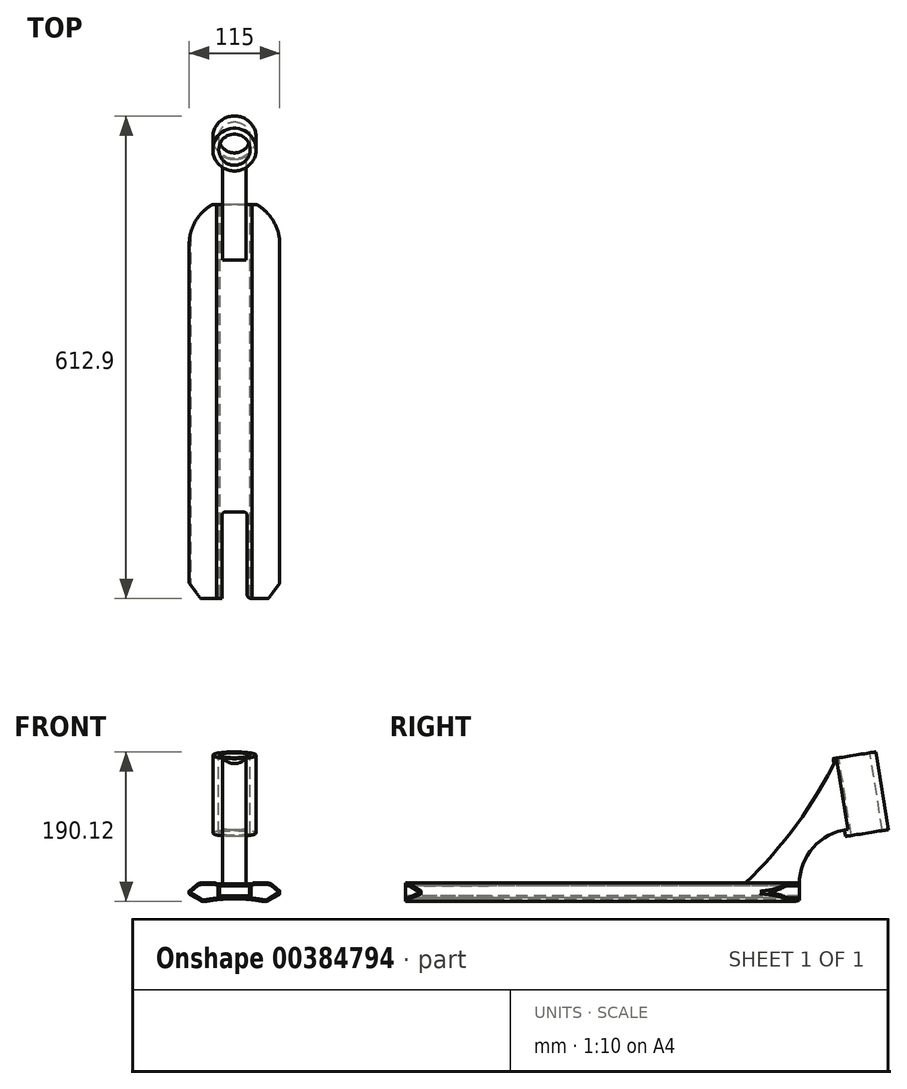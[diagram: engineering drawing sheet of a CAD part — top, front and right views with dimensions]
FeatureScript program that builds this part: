
annotation { "Feature Type Name" : "Feature", "Feature Type Description" : "" }
export const myFeature = defineFeature(function(context is Context, id is Id, definition is map)
    precondition{}
    {
        {
            var Q0;
            Q0=qCreatedBy(makeId("Front.planeOp"),FACE);
            var sketch = newSketch(context, id + "F0", { "sketchPlane" : qUnion([Q0])});
            skLineSegment(sketch, "E0", {"start": v(0, 0) * mm, "end": v(0, 7.07) * mm, "construction": true});
            skLineSegment(sketch, "E1", {"start": v(0, 13.8) * mm, "end": v(22.5, 13.8) * mm});
            skLineSegment(sketch, "E2", {"start": v(22.5, 13.8) * mm, "end": v(22.5, 15.1) * mm});
            skLineSegment(sketch, "E3", {"start": v(22.5, 15.1) * mm, "end": v(45.58, 15.1) * mm});
            skLineSegment(sketch, "E4", {"start": v(45.58, 15.1) * mm, "end": v(57.5, 5.1) * mm});
            skLineSegment(sketch, "E5", {"start": v(57.5, 5.1) * mm, "end": v(57.5, 1.1) * mm});
            skLineSegment(sketch, "E6", {"start": v(57.5, 1.1) * mm, "end": v(40.18, -8.9) * mm});
            skLineSegment(sketch, "E7.MirrorCS", {"start": v(0, 13.8) * mm, "end": v(-22.5, 13.8) * mm});
            skLineSegment(sketch, "E8.MirrorCS", {"start": v(-22.5, 13.8) * mm, "end": v(-22.5, 15.1) * mm});
            skLineSegment(sketch, "E9.MirrorCS", {"start": v(-22.5, 15.1) * mm, "end": v(-45.58, 15.1) * mm});
            skLineSegment(sketch, "E10.MirrorCS", {"start": v(-45.58, 15.1) * mm, "end": v(-57.5, 5.1) * mm});
            skLineSegment(sketch, "E11.MirrorCS", {"start": v(-57.5, 5.1) * mm, "end": v(-57.5, 1.1) * mm});
            skLineSegment(sketch, "E12.MirrorCS", {"start": v(-57.5, 1.1) * mm, "end": v(-40.18, -8.9) * mm});
            skArc(sketch, "E13", {"start": v(40.18, -8.9) * mm, "mid": v(0, -4.83) * mm, "end": v(-40.18, -8.9) * mm});
            skSolve(sketch);
        }
        {
            var Q0;
            Q0 = qSketchRegion(id + "F0", true);
            extrude(context, id + "F1", {"entities" : qUnion([Q0]), "endBound" : BoundingType.SYMMETRIC, "depth" : 500 * mm});
        }
        {
            var Q0;
            Q0=makeQuery(id+"F1.opExtrude","CAP_FACE",FACE,{"disambiguationData":[OSD([sQuery(id+"F0.wireOp",EDGE,"E1"),sQuery(id+"F0.wireOp",EDGE,"E2"),sQuery(id+"F0.wireOp",EDGE,"E3"),sQuery(id+"F0.wireOp",EDGE,"E4"),sQuery(id+"F0.wireOp",EDGE,"E5"),sQuery(id+"F0.wireOp",EDGE,"E6"),sQuery(id+"F0.wireOp",EDGE,"E7.MirrorCS"),sQuery(id+"F0.wireOp",EDGE,"E8.MirrorCS"),sQuery(id+"F0.wireOp",EDGE,"E9.MirrorCS"),sQuery(id+"F0.wireOp",EDGE,"E10.MirrorCS"),sQuery(id+"F0.wireOp",EDGE,"E11.MirrorCS"),sQuery(id+"F0.wireOp",EDGE,"E12.MirrorCS"),sQuery(id+"F0.wireOp",EDGE,"E13")])],"isStart":false});
            var sketch = newSketch(context, id + "F2", { "sketchPlane" : qUnion([Q0])});
            skLineSegment(sketch, "E14.bottom", {"start": v(-19, 11.8) * mm, "end": v(19, 11.8) * mm});
            skLineSegment(sketch, "E14.top", {"start": v(-19, -1.2) * mm, "end": v(19, -1.2) * mm});
            skLineSegment(sketch, "E14.left", {"start": v(-19, 11.8) * mm, "end": v(-19, -1.2) * mm});
            skLineSegment(sketch, "E14.right", {"start": v(19, 11.8) * mm, "end": v(19, -1.2) * mm});
            skSolve(sketch);
        }
        {
            var Q0;
            Q0 = qSketchRegion(id + "F2", true);
            extrude(context, id + "F3", {"entities" : qUnion([Q0]), "operationType" : NewBodyOperationType.REMOVE, "endBound" : BoundingType.THROUGH_ALL, "oppositeDirection" : true, "depth" : 500 * mm});
        }
        {
            var Q0;
            Q0=makeQuery(id+"F1.opExtrude","SWEPT_EDGE",EDGE,{"disambiguationData":[OSD([sQuery(id+"F0.wireOp",EDGE,"E2"),sQuery(id+"F0.wireOp",EDGE,"E3")])]});
            var Q1;
            Q1=makeQuery(id+"F1.opExtrude","SWEPT_EDGE",EDGE,{"disambiguationData":[OSD([sQuery(id+"F0.wireOp",EDGE,"E8.MirrorCS"),sQuery(id+"F0.wireOp",EDGE,"E9.MirrorCS")])]});
            fillet(context, id + "F4", {"entities" : qUnion([Q0, Q1]), "radius" : 2 * mm, "tangentPropagation" : true, "allowEdgeOverflow" : false});
        }
        {
            var Q0;
            Q0=makeQuery(id+"F1.opExtrude","SWEPT_EDGE",EDGE,{"disambiguationData":[OSD([sQuery(id+"F0.wireOp",EDGE,"E3"),sQuery(id+"F0.wireOp",EDGE,"E4")])]});
            var Q1;
            Q1=makeQuery(id+"F1.opExtrude","SWEPT_EDGE",EDGE,{"disambiguationData":[OSD([sQuery(id+"F0.wireOp",EDGE,"E9.MirrorCS"),sQuery(id+"F0.wireOp",EDGE,"E10.MirrorCS")])]});
            var Q2;
            Q2=makeQuery(id+"F1.opExtrude","SWEPT_EDGE",EDGE,{"disambiguationData":[OSD([sQuery(id+"F0.wireOp",EDGE,"E12.MirrorCS"),sQuery(id+"F0.wireOp",EDGE,"E13")])]});
            var Q3;
            Q3=makeQuery(id+"F1.opExtrude","SWEPT_EDGE",EDGE,{"disambiguationData":[OSD([sQuery(id+"F0.wireOp",EDGE,"E6"),sQuery(id+"F0.wireOp",EDGE,"E13")])]});
            fillet(context, id + "F5", {"entities" : qUnion([Q0, Q1, Q2, Q3]), "radius" : 9 * mm, "tangentPropagation" : true, "allowEdgeOverflow" : false});
        }
        {
            var Q0;
            Q0=makeQuery(id+"F1.opExtrude","SWEPT_EDGE",EDGE,{"disambiguationData":[OSD([sQuery(id+"F0.wireOp",EDGE,"E5"),sQuery(id+"F0.wireOp",EDGE,"E6")])]});
            var Q1;
            Q1=makeQuery(id+"F1.opExtrude","SWEPT_EDGE",EDGE,{"disambiguationData":[OSD([sQuery(id+"F0.wireOp",EDGE,"E4"),sQuery(id+"F0.wireOp",EDGE,"E5")])]});
            var Q2;
            Q2=makeQuery(id+"F1.opExtrude","SWEPT_EDGE",EDGE,{"disambiguationData":[OSD([sQuery(id+"F0.wireOp",EDGE,"E10.MirrorCS"),sQuery(id+"F0.wireOp",EDGE,"E11.MirrorCS")])]});
            var Q3;
            Q3=makeQuery(id+"F1.opExtrude","SWEPT_EDGE",EDGE,{"disambiguationData":[OSD([sQuery(id+"F0.wireOp",EDGE,"E11.MirrorCS"),sQuery(id+"F0.wireOp",EDGE,"E12.MirrorCS")])]});
            fillet(context, id + "F6", {"entities" : qUnion([Q0, Q1, Q2, Q3]), "radius" : 1 * mm, "tangentPropagation" : true, "allowEdgeOverflow" : false});
        }
        {
            var Q0;
            Q0=makeQuery(id+"F1.opExtrude","CAP_FACE",FACE,{"disambiguationData":[OSD([sQuery(id+"F0.wireOp",EDGE,"E1"),sQuery(id+"F0.wireOp",EDGE,"E2"),sQuery(id+"F0.wireOp",EDGE,"E3"),sQuery(id+"F0.wireOp",EDGE,"E4"),sQuery(id+"F0.wireOp",EDGE,"E5"),sQuery(id+"F0.wireOp",EDGE,"E6"),sQuery(id+"F0.wireOp",EDGE,"E7.MirrorCS"),sQuery(id+"F0.wireOp",EDGE,"E8.MirrorCS"),sQuery(id+"F0.wireOp",EDGE,"E9.MirrorCS"),sQuery(id+"F0.wireOp",EDGE,"E10.MirrorCS"),sQuery(id+"F0.wireOp",EDGE,"E11.MirrorCS"),sQuery(id+"F0.wireOp",EDGE,"E12.MirrorCS"),sQuery(id+"F0.wireOp",EDGE,"E13")])],"isStart":false});
            var sketch = newSketch(context, id + "F7", { "sketchPlane" : qUnion([Q0])});
            skArc(sketch, "E15.0", {"start": v(37.3, -6.3) * mm, "mid": v(29.18, -4.95) * mm, "end": v(21, -3.92) * mm});
            skArc(sketch, "E15.1", {"start": v(-42.1, -5.49) * mm, "mid": v(-39.78, -6.32) * mm, "end": v(-37.3, -6.3) * mm});
            skLineSegment(sketch, "E15.2", {"start": v(-24.49, 13.1) * mm, "end": v(-42.3, 13.1) * mm});
            skArc(sketch, "E15.3", {"start": v(-42.3, 13.1) * mm, "mid": v(-44.7, 12.67) * mm, "end": v(-46.8, 11.46) * mm});
            skLineSegment(sketch, "E15.4", {"start": v(-46.8, 11.46) * mm, "end": v(-55.76, 3.95) * mm});
            skLineSegment(sketch, "E15.5", {"start": v(-55.61, 2.31) * mm, "end": v(-42.1, -5.49) * mm});
            skPoint(sketch, "E16.visualSharp", {"position": v(-56.85, 3.03) * mm});
            skArc(sketch, "E16.filletArc", {"start": v(-55.76, 3.95) * mm, "mid": v(-56.1, 3.1) * mm, "end": v(-55.61, 2.31) * mm});
            skLineSegment(sketch, "E17", {"start": v(-21, -3.92) * mm, "end": v(-21, 11.8) * mm});
            skLineSegment(sketch, "E18", {"start": v(-21, 11.8) * mm, "end": v(-22.61, 11.8) * mm});
            skArc(sketch, "E19", {"start": v(-22.61, 11.8) * mm, "mid": v(-23.35, 12.74) * mm, "end": v(-24.49, 13.1) * mm});
            skLineSegment(sketch, "E20.MirrorCS", {"start": v(21, -3.92) * mm, "end": v(21, 11.8) * mm});
            skLineSegment(sketch, "E21.MirrorCS", {"start": v(21, 11.8) * mm, "end": v(22.61, 11.8) * mm});
            skArc(sketch, "E22.MirrorCS", {"start": v(22.61, 11.8) * mm, "mid": v(23.35, 12.74) * mm, "end": v(24.49, 13.1) * mm});
            skLineSegment(sketch, "E23.MirrorCS", {"start": v(24.49, 13.1) * mm, "end": v(42.3, 13.1) * mm});
            skArc(sketch, "E24.MirrorCS", {"start": v(42.3, 13.1) * mm, "mid": v(44.7, 12.67) * mm, "end": v(46.8, 11.46) * mm});
            skLineSegment(sketch, "E25.MirrorCS", {"start": v(46.8, 11.46) * mm, "end": v(55.76, 3.95) * mm});
            skArc(sketch, "E26.MirrorCS", {"start": v(55.76, 3.95) * mm, "mid": v(56.1, 3.1) * mm, "end": v(55.61, 2.31) * mm});
            skLineSegment(sketch, "E27.MirrorCS", {"start": v(55.61, 2.31) * mm, "end": v(42.1, -5.49) * mm});
            skArc(sketch, "E28.MirrorCS", {"start": v(42.1, -5.49) * mm, "mid": v(39.78, -6.32) * mm, "end": v(37.3, -6.3) * mm});
            skArc(sketch, "E29.MirrorCS", {"start": v(-37.3, -6.3) * mm, "mid": v(-29.18, -4.95) * mm, "end": v(-21, -3.92) * mm});
            skArc(sketch, "E30.trimOffspring", {"start": v(21, -3.92) * mm, "mid": v(29.18, -4.95) * mm, "end": v(37.3, -6.3) * mm});
            skArc(sketch, "E31.trimOffspring", {"start": v(-21, -3.92) * mm, "mid": v(-29.18, -4.95) * mm, "end": v(-37.3, -6.3) * mm});
            skSolve(sketch);
        }
        {
            var Q0;
            Q0=makeQuery(id+"F7.imprint","IMPRINT",FACE,{"disambiguationData":[TD([[makeQuery(id+"F7.imprint","IMPRINT",EDGE,{"derivedFrom":sQuery(id+"F7.wireOp",EDGE,"E15.1")}),1.0]])]});
            var Q1;
            Q1=makeQuery(id+"F7.imprint","IMPRINT",FACE,{"disambiguationData":[TD([[makeQuery(id+"F7.imprint","IMPRINT",EDGE,{"derivedFrom":sQuery(id+"F7.wireOp",EDGE,"E20.MirrorCS")}),-1.0]])]});
            extrude(context, id + "F8", {"entities" : qUnion([Q0, Q1]), "operationType" : NewBodyOperationType.REMOVE, "endBound" : BoundingType.THROUGH_ALL, "oppositeDirection" : true, "depth" : 25 * mm});
        }
        {
            var Q0;
            Q0=qCreatedBy(makeId("Top.planeOp"),FACE);
            var sketch = newSketch(context, id + "F9", { "sketchPlane" : qUnion([Q0])});
            skArc(sketch, "E32", {"start": v(57.5, 200) * mm, "mid": v(0, 257.5) * mm, "end": v(-57.5, 200) * mm});
            skLineSegment(sketch, "E33", {"start": v(-57.5, 200) * mm, "end": v(-57.5, 280) * mm});
            skLineSegment(sketch, "E34", {"start": v(-57.5, 280) * mm, "end": v(57.5, 280) * mm});
            skLineSegment(sketch, "E35", {"start": v(57.5, 280) * mm, "end": v(57.5, 200) * mm});
            skSolve(sketch);
        }
        {
            var Q0;
            Q0 = qSketchRegion(id + "F9", true);
            extrude(context, id + "F10", {"entities" : qUnion([Q0]), "operationType" : NewBodyOperationType.REMOVE, "endBound" : BoundingType.THROUGH_ALL, "oppositeDirection" : true, "depth" : 25 * mm, "hasSecondDirection" : true, "secondDirectionBound" : SecondDirectionBoundingType.THROUGH_ALL, "secondDirectionOppositeDirection" : false, "secondDirectionDepth" : 25 * mm});
        }
        {
            var Q0;
            Q0=qCreatedBy(makeId("Right.planeOp"),FACE);
            var sketch = newSketch(context, id + "F11", { "sketchPlane" : qUnion([Q0])});
            skLineSegment(sketch, "E36", {"start": v(180, 13.8) * mm, "end": v(250, 13.8) * mm});
            skArc(sketch, "E37", {"start": v(180, 13.8) * mm, "mid": v(245.97, 88.46) * mm, "end": v(297.38, 173.8) * mm});
            skArc(sketch, "E38", {"start": v(311.71, 83.3) * mm, "mid": v(267.66, 60.27) * mm, "end": v(250, 13.8) * mm});
            skLineSegment(sketch, "E39", {"start": v(297.38, 173.8) * mm, "end": v(342.82, 180.99) * mm});
            skLineSegment(sketch, "E40", {"start": v(342.82, 180.99) * mm, "end": v(358.46, 82.22) * mm});
            skLineSegment(sketch, "E41", {"start": v(358.46, 82.22) * mm, "end": v(313.03, 75.03) * mm});
            skLineSegment(sketch, "E42", {"start": v(313.03, 75.03) * mm, "end": v(311.71, 83.3) * mm});
            skSolve(sketch);
        }
        {
            var Q0;
            Q0 = qSketchRegion(id + "F11", true);
            extrude(context, id + "F12", {"entities" : qUnion([Q0]), "operationType" : NewBodyOperationType.ADD, "endBound" : BoundingType.SYMMETRIC, "depth" : 30 * mm});
        }
        {
            var Q0;
            Q0=makeQuery(id+"F12.opExtrude","SWEPT_FACE",FACE,{"disambiguationData":[OSD([sQuery(id+"F11.wireOp",EDGE,"E39")])]});
            var sketch = newSketch(context, id + "F13", { "sketchPlane" : qUnion([Q0])});
            skCircle(sketch, "E43", {"center": v(0, 343.9) * mm, "radius": 27.5 * mm});
            skPoint(sketch, "E43.centerSnap0", {"position": v(0, 320.9) * mm});
            skSolve(sketch);
        }
        {
            var Q0;
            Q0 = qSketchRegion(id + "F13", true);
            var Q1;
            Q1=makeQuery(id+"F12.opExtrude","SWEPT_FACE",FACE,{"disambiguationData":[OSD([sQuery(id+"F11.wireOp",EDGE,"E41")])]});
            extrude(context, id + "F14", {"entities" : qUnion([Q0]), "operationType" : NewBodyOperationType.ADD, "endBound" : BoundingType.UP_TO_SURFACE, "oppositeDirection" : true, "endBoundEntityFace" : qUnion([Q1]), "depth" : 25 * mm});
        }
        {
            var Q0;
            Q0=makeQuery(id+"F14.boolean.opBoolean","MERGE",FACE,{"derivedFrom":[makeQuery(id+"F12.opExtrude","SWEPT_FACE",FACE,{"disambiguationData":[OSD([sQuery(id+"F11.wireOp",EDGE,"E39")])]}),makeQuery(id+"F14.opExtrude","CAP_FACE",FACE,{"disambiguationData":[OSD([sQuery(id+"F13.wireOp",EDGE,"E43")])],"isStart":true})]});
            var sketch = newSketch(context, id + "F15", { "sketchPlane" : qUnion([Q0])});
            skPoint(sketch, "E44", {"position": v(0, 343.9) * mm});
            skSolve(sketch);
        }
        {
            var Q0;
            Q0=sQuery(id+"F15.wireOp",VERTEX,"E44");
            var Q1;
            Q1=makeQuery(id+"F1.opExtrude","SWEPT_BODY",BODY,{"disambiguationData":[OSD([sQuery(id+"F0.wireOp",EDGE,"E1"),sQuery(id+"F0.wireOp",EDGE,"E2"),sQuery(id+"F0.wireOp",EDGE,"E3"),sQuery(id+"F0.wireOp",EDGE,"E4"),sQuery(id+"F0.wireOp",EDGE,"E5"),sQuery(id+"F0.wireOp",EDGE,"E6"),sQuery(id+"F0.wireOp",EDGE,"E7.MirrorCS"),sQuery(id+"F0.wireOp",EDGE,"E8.MirrorCS"),sQuery(id+"F0.wireOp",EDGE,"E9.MirrorCS"),sQuery(id+"F0.wireOp",EDGE,"E10.MirrorCS"),sQuery(id+"F0.wireOp",EDGE,"E11.MirrorCS"),sQuery(id+"F0.wireOp",EDGE,"E12.MirrorCS"),sQuery(id+"F0.wireOp",EDGE,"E13")])]});
            hole(context, id + "F16", {"style" : HoleStyle.SIMPLE, "endStyle" : HoleEndStyle.THROUGH, "holeDiameter" : 40 * mm, "isTappedThrough" : true, "tappedDepth" : 12 * mm, "tapClearance" : 3, "locations" : qUnion([Q0]), "scope" : qUnion([Q1])});
        }
        {
            var Q0;
            Q0=qCreatedBy(makeId("Top.planeOp"),FACE);
            var sketch = newSketch(context, id + "F17", { "sketchPlane" : qUnion([Q0])});
            skLineSegment(sketch, "E45", {"start": v(-68, -216) * mm, "end": v(-68, -346) * mm});
            skLineSegment(sketch, "E46", {"start": v(-68, -346) * mm, "end": v(68, -346) * mm});
            skLineSegment(sketch, "E47", {"start": v(68, -346) * mm, "end": v(68, -216) * mm});
            skLineSegment(sketch, "E48", {"start": v(68, -216) * mm, "end": v(43.3, -250) * mm});
            skLineSegment(sketch, "E49", {"start": v(43.3, -250) * mm, "end": v(16, -250) * mm});
            skLineSegment(sketch, "E50", {"start": v(16, -250) * mm, "end": v(16, -140) * mm});
            skLineSegment(sketch, "E51", {"start": v(16, -140) * mm, "end": v(-16, -140) * mm});
            skLineSegment(sketch, "E52", {"start": v(-16, -140) * mm, "end": v(-16, -250) * mm});
            skLineSegment(sketch, "E53", {"start": v(-16, -250) * mm, "end": v(-43.3, -250) * mm});
            skLineSegment(sketch, "E54", {"start": v(-43.3, -250) * mm, "end": v(-68, -216) * mm});
            skSolve(sketch);
        }
        {
            var Q0;
            Q0 = qSketchRegion(id + "F17", true);
            extrude(context, id + "F18", {"entities" : qUnion([Q0]), "operationType" : NewBodyOperationType.REMOVE, "endBound" : BoundingType.THROUGH_ALL, "oppositeDirection" : true, "depth" : 25 * mm, "hasSecondDirection" : true, "secondDirectionBound" : SecondDirectionBoundingType.THROUGH_ALL, "secondDirectionOppositeDirection" : false, "secondDirectionDepth" : 25 * mm});
        }
        {
            var Q0;
            {var subQ2=sQuery(id+"F17.wireOp",EDGE,"E52");Q0=makeQuery(id+"F18.boolean.opBoolean","COPY",EDGE,{"disambiguationData":[TD([makeQuery(id+"F3.boolean.opBoolean","COPY",FACE,{"derivedFrom":makeQuery(id+"F3.opExtrude","SWEPT_FACE",FACE,{"disambiguationData":[OSD([sQuery(id+"F2.wireOp",EDGE,"E14.bottom")])]})})])],"derivedFrom":makeQuery(id+"F18.opExtrude","SWEPT_EDGE",EDGE,{"disambiguationData":[OSD([subQ2,sQuery(id+"F17.wireOp",EDGE,"E53")])]})});}
            var Q1;
            {var subQ0=sQuery(id+"F17.wireOp",EDGE,"E52");var subQ1=sQuery(id+"F17.wireOp",EDGE,"E51");Q1=makeQuery(id+"F18.boolean.opBoolean","COPY",EDGE,{"disambiguationData":[TD([makeQuery(id+"F1.opExtrude","SWEPT_FACE",FACE,{"disambiguationData":[OSD([sQuery(id+"F0.wireOp",EDGE,"E13")])]})])],"derivedFrom":makeQuery(id+"F18.opExtrude","SWEPT_EDGE",EDGE,{"disambiguationData":[OSD([subQ1,subQ0])]})});}
            var Q2;
            {var subQ0=sQuery(id+"F17.wireOp",EDGE,"E51");var subQ1=sQuery(id+"F17.wireOp",EDGE,"E52");Q2=makeQuery(id+"F18.boolean.opBoolean","COPY",EDGE,{"disambiguationData":[TD([makeQuery(id+"F3.boolean.opBoolean","COPY",FACE,{"derivedFrom":makeQuery(id+"F3.opExtrude","SWEPT_FACE",FACE,{"disambiguationData":[OSD([sQuery(id+"F2.wireOp",EDGE,"E14.bottom")])]})})])],"derivedFrom":makeQuery(id+"F18.opExtrude","SWEPT_EDGE",EDGE,{"disambiguationData":[OSD([subQ0,subQ1])]})});}
            var Q3;
            {var subQ0=sQuery(id+"F17.wireOp",EDGE,"E51");var subQ1=sQuery(id+"F17.wireOp",EDGE,"E50");Q3=makeQuery(id+"F18.boolean.opBoolean","COPY",EDGE,{"disambiguationData":[TD([makeQuery(id+"F3.boolean.opBoolean","COPY",FACE,{"derivedFrom":makeQuery(id+"F3.opExtrude","SWEPT_FACE",FACE,{"disambiguationData":[OSD([sQuery(id+"F2.wireOp",EDGE,"E14.bottom")])]})})])],"derivedFrom":makeQuery(id+"F18.opExtrude","SWEPT_EDGE",EDGE,{"disambiguationData":[OSD([subQ1,subQ0])]})});}
            var Q4;
            {var subQ0=sQuery(id+"F17.wireOp",EDGE,"E50");var subQ1=sQuery(id+"F17.wireOp",EDGE,"E51");Q4=makeQuery(id+"F18.boolean.opBoolean","COPY",EDGE,{"disambiguationData":[TD([makeQuery(id+"F1.opExtrude","SWEPT_FACE",FACE,{"disambiguationData":[OSD([sQuery(id+"F0.wireOp",EDGE,"E13")])]})])],"derivedFrom":makeQuery(id+"F18.opExtrude","SWEPT_EDGE",EDGE,{"disambiguationData":[OSD([subQ0,subQ1])]})});}
            var Q5;
            {var subQ2=sQuery(id+"F17.wireOp",EDGE,"E50");Q5=makeQuery(id+"F18.boolean.opBoolean","COPY",EDGE,{"disambiguationData":[TD([makeQuery(id+"F3.boolean.opBoolean","COPY",FACE,{"derivedFrom":makeQuery(id+"F3.opExtrude","SWEPT_FACE",FACE,{"disambiguationData":[OSD([sQuery(id+"F2.wireOp",EDGE,"E14.bottom")])]})})])],"derivedFrom":makeQuery(id+"F18.opExtrude","SWEPT_EDGE",EDGE,{"disambiguationData":[OSD([sQuery(id+"F17.wireOp",EDGE,"E49"),subQ2])]})});}
            var Q6;
            {var subQ0=sQuery(id+"F0.wireOp",EDGE,"E13");var subQ1=sQuery(id+"F17.wireOp",EDGE,"E50");Q6=makeQuery(id+"F18.boolean.opBoolean","COPY",EDGE,{"disambiguationData":[TD([makeQuery(id+"F1.opExtrude","SWEPT_FACE",FACE,{"disambiguationData":[OSD([subQ0])]})])],"derivedFrom":makeQuery(id+"F18.opExtrude","SWEPT_EDGE",EDGE,{"disambiguationData":[OSD([sQuery(id+"F17.wireOp",EDGE,"E49"),subQ1])]})});}
            var Q7;
            {var subQ0=sQuery(id+"F0.wireOp",EDGE,"E13");var subQ1=sQuery(id+"F17.wireOp",EDGE,"E52");Q7=makeQuery(id+"F18.boolean.opBoolean","COPY",EDGE,{"disambiguationData":[TD([makeQuery(id+"F1.opExtrude","SWEPT_FACE",FACE,{"disambiguationData":[OSD([subQ0])]})])],"derivedFrom":makeQuery(id+"F18.opExtrude","SWEPT_EDGE",EDGE,{"disambiguationData":[OSD([subQ1,sQuery(id+"F17.wireOp",EDGE,"E53")])]})});}
            fillet(context, id + "F19", {"entities" : qUnion([Q0, Q1, Q2, Q3, Q4, Q5, Q6, Q7]), "radius" : 5 * mm, "tangentPropagation" : true, "allowEdgeOverflow" : false});
        }
    });
